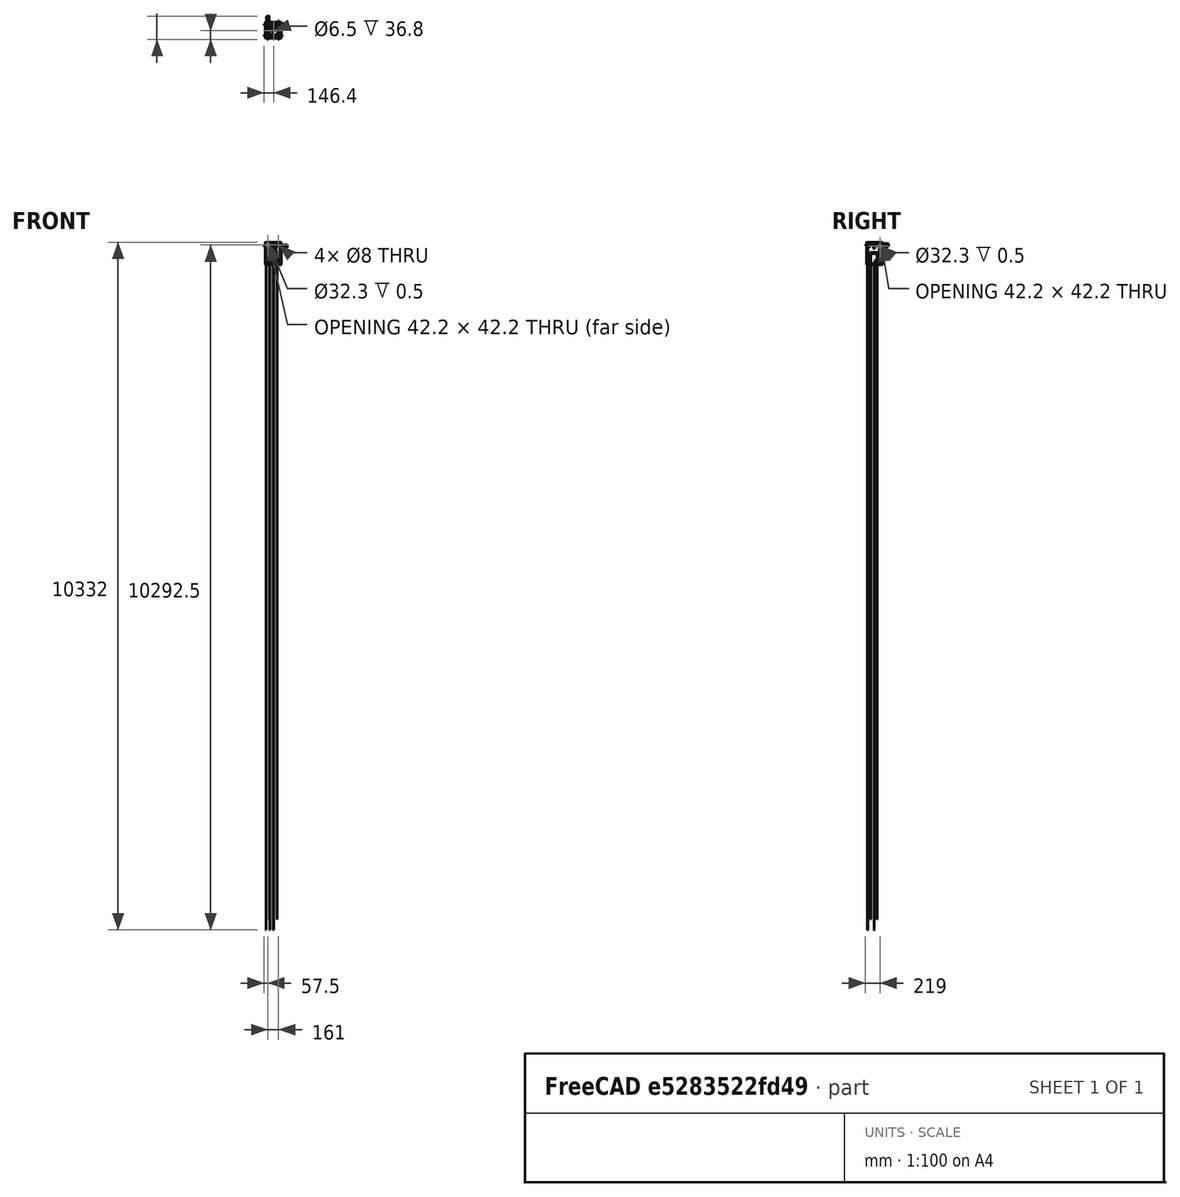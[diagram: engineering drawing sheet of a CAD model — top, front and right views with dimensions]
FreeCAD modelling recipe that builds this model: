
FCSTD DOCUMENT  (FreeCAD 0.14R3702 (Git))
Label: tantillus
License: CC-BY 3.0
LicenseURL: http://creativecommons.org/licenses/by/3.0/
objects: Mesh::Feature×42, Part::Cylinder×42, Part::Cut×35, Part::MultiFuse×16, App::DocumentObjectGroup×15, Part::FeaturePython×15, PartDesign::Pad×12, PartDesign::Chamfer×9, Sketcher::SketchObject×7, PartDesign::Pocket×6, Part::Box×5, Part::Sweep×3, Part::Chamfer×2, PartDesign::Revolution×2, Part::Helix×1
note: 175 computed .brp shape members not serialized (recipe doc carries the construction recipe); baked Part::Feature solids carry a one-line shape summary decoded from their .brp

FEATURE [PartDesign::Pad] Pad  label="Pata001"
  Length = 335
  Length2 = 100
  Type = 0
FEATURE [PartDesign::Pad] Pad001  label="Pata002"
  Length = 335
  Length2 = 100
  Placement = pos=(220,0,0) rot=(0,0,1;0rad)
  Type = 0
FEATURE [PartDesign::Pad] Pad002  label="Pata003"
  Length = 335
  Length2 = 100
  Placement = pos=(0,220,0) rot=(0,0,1;0rad)
  Type = 0
FEATURE [PartDesign::Pad] Pad003  label="Pata004"
  Length = 335
  Length2 = 100
  Placement = pos=(220,220,0) rot=(0,0,1;0rad)
  Type = 0
FEATURE [PartDesign::Pad] Pad004  label="Trab001"
  Length = 200
  Length2 = 100
  Placement = pos=(10,0,10) rot=(0,1,0;1.5708rad)
  Type = 0
FEATURE [Mesh::Feature] panel_combine_BOTTOM
  Placement = pos=(-15,-15,-15) rot=(0.57735,0.57735,0.57735;2.0944rad)
FEATURE [PartDesign::Pad] Pad005  label="Trab002"
  Length = 200
  Length2 = 100
  Placement = pos=(0,10,10) rot=(0.57735,-0.57735,-0.57735;4.18879rad)
  Type = 0
FEATURE [Mesh::Feature] panel_combine_BOTTOM001
  Placement = pos=(-15,235,-15) rot=(1,0,0;1.5708rad)
FEATURE [Mesh::Feature] panel_combine_BOTTOM002
  Placement = pos=(235,-15,-15) rot=(0,0.707107,0.707107;3.14159rad)
FEATURE [Mesh::Feature] panel_combine_BOTTOM003
  Placement = pos=(235,235,-15) rot=(0.57735,-0.57735,-0.57735;2.0944rad)
FEATURE [PartDesign::Pad] Pad006  label="Trab003"
  Length = 200
  Length2 = 100
  Placement = pos=(220,10,10) rot=(0.57735,-0.57735,-0.57735;4.18879rad)
  Type = 0
FEATURE [PartDesign::Pad] Pad007  label="Trab004"
  Length = 200
  Length2 = 100
  Placement = pos=(10,220,10) rot=(0,1,0;1.5708rad)
  Type = 0
FEATURE [PartDesign::Pad] Pad008  label="Trab005"
  Length = 200
  Length2 = 100
  Placement = pos=(10,0,325) rot=(0,1,0;1.5708rad)
  Type = 0
FEATURE [PartDesign::Pad] Pad009  label="Trab006"
  Length = 200
  Length2 = 100
  Placement = pos=(0,10,325) rot=(0.57735,-0.57735,-0.57735;4.18879rad)
  Type = 0
FEATURE [PartDesign::Pad] Pad010  label="Trab007"
  Length = 200
  Length2 = 100
  Placement = pos=(220,10,325) rot=(0.57735,-0.57735,-0.57735;4.18879rad)
  Type = 0
FEATURE [PartDesign::Pad] Pad011  label="Trab008"
  Length = 200
  Length2 = 100
  Placement = pos=(10,220,325) rot=(0,1,0;1.5708rad)
  Type = 0
FEATURE [Mesh::Feature] AnguloFrontDerecho
  Placement = pos=(50,-26,333) rot=(0,1,0;3.14159rad)
FEATURE [Mesh::Feature] AnguloFrontIzquierdo
  Placement = pos=(170.5,77,331) rot=(1,0,0;3.14159rad)
FEATURE [Mesh::Feature] AnguloTraseroDerecho
  Placement = pos=(50,143,331) rot=(0,1,0;3.14159rad)
FEATURE [Mesh::Feature] AnguloTraseroIzq
  Placement = pos=(240,162,331) rot=(0,1,0;3.14159rad)
FEATURE [App::DocumentObjectGroup] Grupo  label="T-Slot"
  Group = -> [Pad006,Pad007,Pad008,Pad009,Pad010,Pad011,Pad005,Pad,Pad001,Pad002,Pad003,Pad004]
FEATURE [App::DocumentObjectGroup] Grupo001  label="AngulosSup"
  Group = -> [AnguloFrontDerecho,AnguloFrontIzquierdo,AnguloTraseroDerecho,AnguloTraseroIzq]
FEATURE [App::DocumentObjectGroup] Grupo002  label="AngulosInf"
  Group = -> [panel_combine_BOTTOM,panel_combine_BOTTOM001,panel_combine_BOTTOM002,panel_combine_BOTTOM003]
FEATURE [Mesh::Feature] z_upper_adapter_long
  Placement = pos=(102,256.5,333) rot=(1,0,0;3.14159rad)
FEATURE [Mesh::Feature] z_lower_adapter
  Placement = pos=(122,233,-27) rot=(0,0,1;3.14159rad)
FEATURE [PartDesign::Chamfer] Chamfer001
  Placement = pos=(29.5,234,295.5) rot=(0,0,1;0rad)
  Size = 0.25
FEATURE [PartDesign::Chamfer] Chamfer
  Placement = pos=(29.5,-14,295.5) rot=(0,0,1;0rad)
  Size = 0.25
FEATURE [PartDesign::Chamfer] Chamfer002
  Placement = pos=(190.5,-14,295.5) rot=(0,0,1;0rad)
  Size = 0.25
FEATURE [PartDesign::Chamfer] Chamfer003
  Placement = pos=(190.5,234,295.5) rot=(0,0,1;0rad)
  Size = 0.25
FEATURE [App::DocumentObjectGroup] Grupo003  label="rodamientosX"
  Group = -> [Chamfer001,Chamfer,Chamfer002,Chamfer003]
FEATURE [PartDesign::Chamfer] Chamfer004
  Placement = pos=(-14,29.5,275.5) rot=(0,0,1;1.5708rad)
  Size = 0.25
FEATURE [PartDesign::Chamfer] Chamfer005
  Placement = pos=(234.5,29.5,275.5) rot=(0,0,1;1.5708rad)
  Size = 0.25
FEATURE [PartDesign::Chamfer] Chamfer006
  Placement = pos=(234.5,191,275.5) rot=(0,0,1;1.5708rad)
  Size = 0.25
FEATURE [PartDesign::Chamfer] Chamfer007
  Placement = pos=(-14,191,275.5) rot=(0,0,1;1.5708rad)
  Size = 0.25
FEATURE [App::DocumentObjectGroup] Grupo004  label="rodamientosY"
  Group = -> [Chamfer004,Chamfer005,Chamfer006,Chamfer007]
FEATURE [PartDesign::Pocket] Pocket006
  Length = 3
  Type = 0
FEATURE [Part::FeaturePython] refine  label="motor"  # WARN: FeaturePython — macro-defined, semantics opaque (R4)
  Base = -> Pocket006
  Placement = pos=(322,191,275.5) rot=(0,-1,0;1.5708rad)
FEATURE [Part::Cylinder] Cylinder  label="Cilindro"
  Angle = 360
  Height = 40
  Placement = pos=(0,0,0) rot=(0,1,0;1.5708rad)
  Radius = 2.5
FEATURE [Part::Cylinder] Cylinder001  label="Cilindro001"
  Angle = 360
  Height = 44
  Placement = pos=(-2,0,0) rot=(0,1,0;1.5708rad)
  Radius = 1.5
FEATURE [Part::Cut] Cut  label="soporte1"
  Base = -> Cylinder
  Placement = pos=(235,175.5,291) rot=(0,0,1;0rad)
  Tool = -> Cylinder001
FEATURE [Part::Cylinder] Cylinder002  label="Cilindro002"
  Angle = 360
  Height = 40
  Placement = pos=(0,0,0) rot=(0,1,0;1.5708rad)
  Radius = 2.5
FEATURE [Part::Cylinder] Cylinder003  label="Cilindro003"
  Angle = 360
  Height = 44
  Placement = pos=(-2,0,0) rot=(0,1,0;1.5708rad)
  Radius = 1.5
FEATURE [Part::Cut] Cut001  label="soporte2"
  Base = -> Cylinder002
  Placement = pos=(235,206.5,291) rot=(0,0,1;0rad)
  Tool = -> Cylinder003
FEATURE [Part::Cylinder] Cylinder004  label="Cilindro004"
  Angle = 360
  Height = 40
  Placement = pos=(0,0,0) rot=(0,1,0;1.5708rad)
  Radius = 2.5
FEATURE [Part::Cylinder] Cylinder005  label="Cilindro005"
  Angle = 360
  Height = 44
  Placement = pos=(-2,0,0) rot=(0,1,0;1.5708rad)
  Radius = 1.5
FEATURE [Part::Cut] Cut002  label="soporte3"
  Base = -> Cylinder004
  Placement = pos=(235,175.5,260) rot=(0,0,1;0rad)
  Tool = -> Cylinder005
FEATURE [Part::Cylinder] Cylinder006  label="Cilindro006"
  Angle = 360
  Height = 40
  Placement = pos=(0,0,0) rot=(0,1,0;1.5708rad)
  Radius = 2.5
FEATURE [Part::Cylinder] Cylinder007  label="Cilindro007"
  Angle = 360
  Height = 44
  Placement = pos=(-2,0,0) rot=(0,1,0;1.5708rad)
  Radius = 1.5
FEATURE [Part::Cut] Cut003  label="soporte4"
  Base = -> Cylinder006
  Placement = pos=(235,206.5,260) rot=(0,0,1;0rad)
  Tool = -> Cylinder007
FEATURE [Part::Cylinder] Cylinder008  label="barraM8Ymotor"
  Angle = 360
  Height = 276
  Placement = pos=(-28,191,275.5) rot=(0,1,0;1.5708rad)
  Radius = 4
FEATURE [Mesh::Feature] Ruedecilla
  Placement = pos=(-37,178.5,281) rot=(0,1,0;1.5708rad)
FEATURE [Part::Cut] Cut004  label="soporte005"
  Base = -> Cylinder004
  Placement = pos=(45,235,280) rot=(0,0,1;1.5708rad)
  Tool = -> Cylinder005
FEATURE [Part::Cut] Cut005  label="soporte006"
  Base = -> Cylinder002
  Placement = pos=(14,235,311) rot=(0,0,1;1.5708rad)
  Tool = -> Cylinder003
FEATURE [Part::Cut] Cut006  label="soporte007"
  Base = -> Cylinder
  Placement = pos=(45,235,311) rot=(0,0,1;1.5708rad)
  Tool = -> Cylinder001
FEATURE [Part::FeaturePython] refine001  label="motor001"  # WARN: FeaturePython — macro-defined, semantics opaque (R4)
  Base = -> Pocket006
  Placement = pos=(29.5,322,295.5) rot=(0.57735,-0.57735,0.57735;2.0944rad)
FEATURE [Part::Cut] Cut007  label="soporte008"
  Base = -> Cylinder006
  Placement = pos=(14,235,280) rot=(0,0,1;1.5708rad)
  Tool = -> Cylinder007
FEATURE [Mesh::Feature] Ruedecilla001
  Placement = pos=(42,-37,301) rot=(0.57735,-0.57735,-0.57735;4.18879rad)
FEATURE [Part::Cylinder] Cylinder009  label="barraM8Xmotor"
  Angle = 360
  Height = 276
  Placement = pos=(29.5,-28,295.5) rot=(-0.57735,0.57735,0.57735;2.0944rad)
  Radius = 4
FEATURE [Part::Cylinder] Cylinder010  label="barraM8Y"
  Angle = 360
  Height = 276
  Placement = pos=(-28,29.5,275.5) rot=(0,1,0;1.5708rad)
  Radius = 4
FEATURE [Mesh::Feature] Ruedecilla002
  Placement = pos=(-37,17,281) rot=(0,1,0;1.5708rad)
FEATURE [Part::Cylinder] Cylinder011  label="barraM8X"
  Angle = 360
  Height = 276
  Placement = pos=(190.5,-28,295.5) rot=(0.57735,-0.57735,-0.57735;4.18879rad)
  Radius = 4
FEATURE [Mesh::Feature] Ruedecilla003
  Placement = pos=(203,-37,301) rot=(0.57735,-0.57735,-0.57735;4.18879rad)
FEATURE [Mesh::Feature] Ruedecilla004
  Placement = pos=(257,17,270) rot=(0,-1,0;1.5708rad)
FEATURE [Mesh::Feature] Ruedecilla005
  Placement = pos=(203,257,290) rot=(0.57735,-0.57735,0.57735;2.0944rad)
FEATURE [App::DocumentObjectGroup] Grupo006  label="barras"
  Group = -> [Cylinder008,Ruedecilla,Cylinder009,Ruedecilla001,Cylinder010,Ruedecilla002,Cylinder011,Ruedecilla003,Ruedecilla004,Ruedecilla005]
FEATURE [Mesh::Feature] Bowden_clamp  label="Bowden clamp"
  Placement = pos=(118.4,102,304.5) rot=(0,0,1;0rad)
FEATURE [Mesh::Feature] printable_lm8uu_v  label="printable-lm8uu1"
  Placement = pos=(110.3,122.1,282.6) rot=(0.57735,-0.57735,-0.57735;2.0944rad)
FEATURE [Mesh::Feature] Carriage_bottom  label="Carriage bottom"
  Placement = pos=(-12.5,110.5,285.5) rot=(0,1,0;1.5708rad)
FEATURE [Mesh::Feature] Carriage_top  label="Carriage top"
  Placement = pos=(112.3,233,285.5) rot=(0.57735,0.57735,-0.57735;2.0944rad)
FEATURE [Mesh::Feature] printable_lm8uu_v001  label="printable-lm8uu2"
  Placement = pos=(106.2,108,296.1) rot=(0.57735,0.57735,-0.57735;2.0944rad)
FEATURE [Part::Cylinder] Cylinder012  label="barraX"
  Angle = 360
  Height = 175
  Placement = pos=(100,198,294.5) rot=(0.57735,0.57735,-0.57735;2.0944rad)
  Radius = 4
FEATURE [Part::Cylinder] Cylinder013  label="barraY"
  Angle = 360
  Height = 175
  Placement = pos=(197.3,120.5,276.4) rot=(0.57735,-0.57735,-0.57735;2.0944rad)
  Radius = 4
FEATURE [App::DocumentObjectGroup] Grupo009  label="carro"
  Group = -> [Bowden_clamp,printable_lm8uu_v,Carriage_bottom,Carriage_top,printable_lm8uu_v001,Cylinder012,Cylinder013]
FEATURE [Mesh::Feature] XY_end_left
  Placement = pos=(-23,-51.5,255) rot=(0,1,0;1.5708rad)
FEATURE [Mesh::Feature] XY_end_right
  Placement = pos=(110,110,163) rot=(0,0,1;0rad)
FEATURE [Mesh::Feature] printable_lm8uu_v002  label="printable-lm8uu003"
  Placement = pos=(105,31.1,281.8) rot=(0.57735,-0.57735,-0.57735;2.0944rad)
FEATURE [Mesh::Feature] printable_lm8uu_v003  label="printable-lm8uu004"
  Placement = pos=(106,192.6,281.7) rot=(0.57735,-0.57735,-0.57735;2.0944rad)
FEATURE [Mesh::Feature] printable_lm8uu_v004  label="printable-lm8uu005"
  Placement = pos=(27.9,114.5,289.3) rot=(-1,0,0;1.5708rad)
FEATURE [Mesh::Feature] printable_lm8uu_v005  label="printable-lm8uu006"
  Placement = pos=(188.9,115.5,289.2) rot=(-1,0,0;1.5708rad)
FEATURE [Mesh::Feature] XY_end_right001
  Placement = pos=(110.5,110.5,408) rot=(0.707107,-0.707107,0;3.14159rad)
FEATURE [Mesh::Feature] XY_end_left001
  Placement = pos=(271.5,243.5,316) rot=(0.57735,-0.57735,0.57735;2.0944rad)
FEATURE [App::DocumentObjectGroup] Grupo010  label="estremos"
  Group = -> [XY_end_left,XY_end_right,printable_lm8uu_v002,printable_lm8uu_v003,printable_lm8uu_v004,printable_lm8uu_v005,XY_end_right001,XY_end_left001]
FEATURE [Mesh::Feature] SoporteMotorEjeYFijo  label="SoporteMotorEjeZFijo"
  Placement = pos=(69,210.5,20) rot=(0,0,-1;1.5708rad)
FEATURE [Mesh::Feature] SoporteSuperiorEjeYFijo  label="SoporteSuperiorEjeZFijo"
  Placement = pos=(69,210,95) rot=(0,0,-1;1.5708rad)
FEATURE [Part::Cylinder] Cylinder014  label="barraM8008"
  Angle = 360
  Height = 225
  Placement = pos=(77,183.3,23) rot=(0,0,1;0rad)
  Radius = 4
FEATURE [Part::Cylinder] Cylinder015  label="barraM8009"
  Angle = 360
  Height = 225
  Placement = pos=(147,183.3,23) rot=(0,0,1;0rad)
  Radius = 4
FEATURE [Mesh::Feature] Z_arm_  label="Z_arm_1"
  Placement = pos=(87,108,88) rot=(0.57735,-0.57735,-0.57735;2.0944rad)
FEATURE [Mesh::Feature] Z_arm_001  label="Z_arm_2"
  Placement = pos=(137,108,88) rot=(0.57735,-0.57735,0.57735;4.18879rad)
FEATURE [Mesh::Feature] Z_lift
  Placement = pos=(107,253.5,219.1) rot=(0,0,1;1.5708rad)
FEATURE [Mesh::Feature] printable_lm8uu_v006  label="printable-lm8uu-v3"
  Placement = pos=(145.3,189.5,110) rot=(0,0,1;0rad)
FEATURE [Mesh::Feature] printable_lm8uu_v007  label="printable-lm8uu-v004"
  Placement = pos=(145.3,189.5,163) rot=(0,0,1;0rad)
FEATURE [Mesh::Feature] printable_lm8uu_v008  label="printable-lm8uu-v005"
  Placement = pos=(75.4,189.5,163) rot=(0,0,1;0rad)
FEATURE [Mesh::Feature] printable_lm8uu_v009  label="printable-lm8uu-v006"
  Placement = pos=(75.4,189.5,110) rot=(0,0,1;0rad)
FEATURE [Part::Box] Box  label="tablelisa"
  Height = 3
  Length = 120
  Placement = pos=(53,45,161) rot=(0,0,1;0rad)
  Width = 120
FEATURE [Part::FeaturePython] refine002  label="motor002"  # WARN: FeaturePython — macro-defined, semantics opaque (R4)
  Placement = pos=(123.06,123.895,42) rot=(-0.987266,-0.112485,0.112485;1.58361rad)
FEATURE [Mesh::Feature] Z_lift001
  Placement = pos=(96,90,163.6) rot=(0,0,-1;1.5708rad)
FEATURE [Mesh::Feature] Z_lift_tensioner
  Placement = pos=(113,239.7,126.3) rot=(0.519988,-0.519988,-0.677661;1.95044rad)
FEATURE [App::DocumentObjectGroup] Grupo012  label="lift cordel"
  Group = -> [Z_lift001,Z_lift_tensioner]
FEATURE [Part::Cylinder] Cylinder016  label="Cilindro008"
  Angle = 360
  Height = 10
  Placement = pos=(79.5,114.1,158) rot=(0,0,1;0rad)
  Radius = 2.6
FEATURE [Part::Cylinder] Cylinder017  label="Cilindro009"
  Angle = 360
  Height = 10
  Placement = pos=(144.5,114.1,158) rot=(0,0,1;0rad)
  Radius = 2.6
FEATURE [Part::Cylinder] Cylinder018  label="Cilindro010"
  Angle = 360
  Height = 10
  Placement = pos=(144.5,152.1,158) rot=(0,0,1;0rad)
  Radius = 2.6
FEATURE [Part::Cylinder] Cylinder019  label="Cilindro011"
  Angle = 360
  Height = 10
  Placement = pos=(79.5,152.1,158) rot=(0,0,1;0rad)
  Radius = 2.6
FEATURE [Part::Cut] Cut008
  Base = -> Box
  Tool = -> Cylinder016
FEATURE [Part::Cut] Cut009
  Base = -> Cut008
  Tool = -> Cylinder017
FEATURE [Part::Cut] Cut010
  Base = -> Cut009
  Tool = -> Cylinder019
FEATURE [Part::Cut] Cut011  label="mesainf01"
  Base = -> Cut010
  Tool = -> Cylinder018
FEATURE [Part::Box] Box001  label="tablelisa001"
  Height = 3
  Length = 120
  Placement = pos=(53,45,174) rot=(0,0,1;0rad)
  Width = 120
FEATURE [Sketcher::SketchObject] Sketch
  Placement = pos=(53,45,177) rot=(0,0,1;0rad)
  Support = -> Box001 [Face6]
  sketch-geometry (3):
    g0: Circle CenterX=5 CenterY=5 CenterZ=0 NormalX=0 NormalY=0 NormalZ=1 Radius=1.5
    g1: Circle CenterX=115 CenterY=5 CenterZ=0 NormalX=0 NormalY=0 NormalZ=1 Radius=1.5
    g2: Circle CenterX=60 CenterY=105 CenterZ=0 NormalX=0 NormalY=0 NormalZ=1 Radius=1.5
  constraints (9):
    c: Equal(g2,g1)
    c: Equal(g1,g0)
    c: Radius(g0) = 1.5
    c: DistanceY(g-1,g0) = 5
    c: DistanceX(g-1,g0) = 5
    c: DistanceY(g-1,g1) = 5
    c: DistanceX(g-1,g1) = 115
    c: DistanceY(g-1,g2) = 105
    c: DistanceX(g-1,g2) = 60
FEATURE [PartDesign::Pocket] Pocket  label="mesasup"
  Length = 5
  Placement = pos=(53,45,174) rot=(0,0,1;0rad)
  Sketch = -> Sketch
  Type = 1
FEATURE [Sketcher::SketchObject] Sketch001
  ExternalGeometry = -> [Cut011]
  Placement = pos=(0,0,164) rot=(0,0,1;0rad)
  Support = -> Cut011 [Face3]
  sketch-geometry (3):
    g0: Circle CenterX=58 CenterY=50 CenterZ=0 NormalX=0 NormalY=0 NormalZ=1 Radius=1.5
    g1: Circle CenterX=168 CenterY=50 CenterZ=0 NormalX=0 NormalY=0 NormalZ=1 Radius=1.5
    g2: Circle CenterX=113 CenterY=150 CenterZ=0 NormalX=0 NormalY=0 NormalZ=1 Radius=1.5
  constraints (9):
    c: Equal(g2,g1)
    c: Equal(g1,g0)
    c: Radius(g1) = 1.5
    c: DistanceX(g0,g-4) = -5
    c: DistanceY(g0,g-4) = -5
    c: DistanceX(g1,g-4) = 5
    c: DistanceY(g1,g-4) = -5
    c: DistanceX(g2,g-3) = -60
    c: DistanceY(g2,g-3) = 15
FEATURE [PartDesign::Pocket] Pocket007  label="mesainf"
  Length = 5
  Sketch = -> Sketch001
  Type = 1
FEATURE [Part::Cylinder] Cylinder020  label="Cilindro012"
  Angle = 360
  Height = 22
  Radius = 1.5
FEATURE [Part::Chamfer] Chamfer008
  Base = -> Cylinder020
  Edges = 1 edges r=0.2: [Edge3]
FEATURE [Part::Cylinder] Cylinder021  label="Cilindro013"
  Angle = 360
  Height = 3
  Placement = pos=(0,0,21) rot=(0,0,1;0rad)
  Radius = 2
FEATURE [Part::Chamfer] Chamfer009
  Base = -> Cylinder021
  Edges = 1 edges r=0.2: [Edge1]
FEATURE [Part::MultiFuse] Fusion
  Shapes = -> [Chamfer008,Chamfer009]
FEATURE [Sketcher::SketchObject] Sketch002
  Placement = pos=(0,0,24) rot=(0,0,1;0rad)
  Support = -> Fusion [Face7]
  sketch-geometry (7):
    g0: LineSegment StartX=-1.25 StartY=0.721688 StartZ=0 EndX=0 EndY=1.44338 EndZ=0
    g1: LineSegment StartX=0 StartY=1.44338 StartZ=0 EndX=1.25 EndY=0.721688 EndZ=0
    g2: LineSegment StartX=1.25 StartY=0.721688 StartZ=0 EndX=1.25 EndY=-0.721688 EndZ=0
    g3: LineSegment StartX=1.25 StartY=-0.721688 StartZ=0 EndX=0 EndY=-1.44338 EndZ=0
    g4: LineSegment StartX=0 StartY=-1.44338 StartZ=0 EndX=-1.25 EndY=-0.721688 EndZ=0
    g5: LineSegment StartX=-1.25 StartY=-0.721688 StartZ=0 EndX=-1.25 EndY=0.721688 EndZ=0
    g6: LineSegment [constr] StartX=0 StartY=1.44338 StartZ=0 EndX=0 EndY=0 EndZ=0
  constraints (20):
    c: PointOnObject(g0,g-2)
    c: Coincident(g0,g1)
    c: Coincident(g1,g2)
    c: Vertical(g2)
    c: Coincident(g2,g3)
    c: PointOnObject(g3,g-2)
    c: Coincident(g3,g4)
    c: Coincident(g4,g5)
    c: Coincident(g5,g0)
    c: Vertical(g5)
    c: Equal(g5,g0)
    c: Equal(g0,g1)
    c: Equal(g1,g2)
    c: Equal(g2,g3)
    c: Equal(g3,g4)
    c: Coincident(g6,g0)
    c: Coincident(g6,g-1)
    c: Angle(g0,g6) = 1.0472
    c: Symmetric(g0,g3,g-1)
    c: DistanceX(g2,g4) = -2.5
FEATURE [PartDesign::Pocket] Pocket008
  Length = 2
  Sketch = -> Sketch002
  Type = 0
FEATURE [Part::Cylinder] Cylinder022  label="Cilindro014"
  Angle = 360
  Height = 0.3
  Placement = pos=(0,0,20.7) rot=(0,0,1;0rad)
  Radius = 3
FEATURE [Part::MultiFuse] Fusion001
  Shapes = -> [Cylinder022,Pocket008]
FEATURE [Part::Cylinder] Cylinder023  label="Cilindro015"
  Angle = 360
  Height = 0.3
  Placement = pos=(0,0,17.4) rot=(0,0,1;0rad)
  Radius = 3
FEATURE [Part::MultiFuse] Fusion002
  Shapes = -> [Cylinder023,Fusion001]
FEATURE [Part::Cylinder] Cylinder024  label="Cilindro016"
  Angle = 360
  Height = 0.3
  Placement = pos=(0,0,7.7) rot=(0,0,1;0rad)
  Radius = 3
FEATURE [Part::MultiFuse] Fusion003
  Shapes = -> [Cylinder024,Fusion002]
FEATURE [Part::Cylinder] Cylinder025  label="Cilindro017"
  Angle = 360
  Height = 0.3
  Placement = pos=(0,0,4.4) rot=(0,0,1;0rad)
  Radius = 3
FEATURE [Part::MultiFuse] Fusion004
  Shapes = -> [Fusion003,Cylinder025]
FEATURE [Part::Helix] Helix  label="Muelletrazo"
  Angle = 0
  Height = 9.4
  LocalCoord = 0
  Pitch = 1
  Placement = pos=(0,0,8) rot=(0,0,1;0rad)
  Radius = 2.5
  Style = 1
FEATURE [Sketcher::SketchObject] Sketch003
  Placement = pos=(0,0,0) rot=(1,0,0;1.5708rad)
  sketch-geometry (1):
    g0: Circle CenterX=2.5 CenterY=8 CenterZ=0 NormalX=0 NormalY=0 NormalZ=1 Radius=0.1
  constraints (3):
    c: Radius(g0) = 0.1
    c: DistanceX(g-1,g0) = 2.5
    c: DistanceY(g-1,g0) = 8
FEATURE [Part::Sweep] Sweep
  Frenet = true
  Sections = -> [Sketch003]
  Solid = true
  Spine = -> Helix [Edge1]
  Transition = 1
FEATURE [Part::MultiFuse] Fusion005  label="tonillocama"
  Placement = pos=(58,50,156.3) rot=(0,0,1;0rad)
  Shapes = -> [Fusion004,Sweep]
FEATURE [Part::Sweep] Sweep001
  Frenet = true
  Sections = -> [Sketch003]
  Solid = true
  Spine = -> Helix [Edge1]
  Transition = 1
FEATURE [Part::MultiFuse] Fusion006
  Shapes = -> [Fusion003,Cylinder025]
FEATURE [Part::MultiFuse] Fusion007  label="tonillocama001"
  Placement = pos=(168,50,156.3) rot=(0,0,1;0rad)
  Shapes = -> [Fusion006,Sweep001]
FEATURE [Part::MultiFuse] Fusion008
  Shapes = -> [Fusion003,Cylinder025]
FEATURE [Part::Sweep] Sweep002
  Frenet = true
  Sections = -> [Sketch003]
  Solid = true
  Spine = -> Helix [Edge1]
  Transition = 1
FEATURE [Part::MultiFuse] Fusion009  label="tonillocama002"
  Placement = pos=(113,150,156.3) rot=(0,0,1;0rad)
  Shapes = -> [Fusion008,Sweep002]
FEATURE [Part::Cylinder] Cylinder026  label="Cilindro018"
  Angle = 360
  Height = 3
  Radius = 7
FEATURE [Sketcher::SketchObject] Sketch004  label="PasoTuerca"
  Placement = pos=(0,0,3) rot=(0,0,1;0rad)
  Support = -> Cylinder026 [Face2]
  sketch-geometry (8):
    g0: LineSegment StartX=-3.46409 StartY=0 StartZ=0 EndX=-1.73205 EndY=3 EndZ=0
    g1: LineSegment StartX=-1.73205 StartY=3 StartZ=0 EndX=1.73205 EndY=3 EndZ=0
    g2: LineSegment StartX=1.73205 StartY=3 StartZ=0 EndX=3.46409 EndY=0 EndZ=0
    g3: LineSegment StartX=3.46409 StartY=0 StartZ=0 EndX=1.73205 EndY=-3 EndZ=0
    g4: LineSegment StartX=1.73205 StartY=-3 StartZ=0 EndX=-1.73205 EndY=-3 EndZ=0
    g5: LineSegment StartX=-1.73205 StartY=-3 StartZ=0 EndX=-3.46409 EndY=0 EndZ=0
    g6: LineSegment [constr] StartX=-3.46409 StartY=0 StartZ=0 EndX=0 EndY=0 EndZ=0
    g7: LineSegment [constr] StartX=-1.73205 StartY=3 StartZ=0 EndX=0 EndY=0 EndZ=0
  constraints (21):
    c: Coincident(g0,g1)
    c: Coincident(g1,g2)
    c: Coincident(g2,g3)
    c: Coincident(g3,g4)
    c: Coincident(g4,g5)
    c: Coincident(g5,g0)
    c: Equal(g5,g0)
    c: Equal(g0,g1)
    c: Equal(g1,g2)
    c: Equal(g2,g3)
    c: Equal(g3,g4)
    c: Coincident(g6,g0)
    c: Horizontal(g1)
    c: Horizontal(g4)
    c: DistanceY(g0,g4) = -6
    c: Symmetric(g4,g0,g6)
    c: Symmetric(g0,g2,g6)
    c: Coincident(g7,g0)
    c: Coincident(g7,g6)
    c: Angle(g7,g6) = 1.0472
    c: Coincident(g6,g-1)
FEATURE [PartDesign::Pocket] Pocket009
  Length = 2
  Sketch = -> Sketch004
  Type = 0
FEATURE [App::DocumentObjectGroup] Grupo013  label="ocultar"
  Group = -> [Box,Z_lift,Box001,Cut011,Fusion,Helix,Pocket009,Cylinder026]
FEATURE [PartDesign::Chamfer] Chamfer010
  Base = -> Pocket009 [Edge1]
  Size = 1
FEATURE [Part::Cylinder] Cylinder027  label="Cilindro019"
  Angle = 360
  Height = 10
  Placement = pos=(0,0,-2) rot=(0,0,1;0rad)
  Radius = 1.5
FEATURE [Part::Cut] Cut012
  Base = -> Chamfer010
  Tool = -> Cylinder027
FEATURE [Part::Cylinder] Cylinder028  label="Cilindro020"
  Angle = 360
  Height = 10
  Placement = pos=(7,0,-2) rot=(0,0,1;0rad)
  Radius = 1
FEATURE [Part::FeaturePython] Array  # Draft array (typed FeaturePython)
  Angle = 360
  ArrayType = 1
  Axis = (0,0,1)
  Base = -> Cylinder028
  Center = (0,0,0)
  IntervalX = (1,0,0)
  IntervalY = (0,1,0)
  IntervalZ = (0,0,1)
  NumberPolar = 12
  NumberX = 2
  NumberY = 2
  NumberZ = 1
FEATURE [Part::Cut] Cut013
  Base = -> Cut012
  Placement = pos=(58,50,157) rot=(0,0,1;0rad)
  Tool = -> Array
FEATURE [Part::Cut] Cut014
  Base = -> Chamfer010
  Tool = -> Cylinder027
FEATURE [Part::FeaturePython] Array001  # Draft array (typed FeaturePython)
  Angle = 360
  ArrayType = 1
  Axis = (0,0,1)
  Base = -> Cylinder028
  Center = (0,0,0)
  IntervalX = (1,0,0)
  IntervalY = (0,1,0)
  IntervalZ = (0,0,1)
  NumberPolar = 12
  NumberX = 2
  NumberY = 2
  NumberZ = 1
FEATURE [Part::Cut] Cut015
  Base = -> Cut014
  Placement = pos=(168,50,157) rot=(0,0,1;0rad)
  Tool = -> Array001
FEATURE [Part::Cut] Cut016
  Base = -> Chamfer010
  Tool = -> Cylinder027
FEATURE [Part::FeaturePython] Array002  # Draft array (typed FeaturePython)
  Angle = 360
  ArrayType = 1
  Axis = (0,0,1)
  Base = -> Cylinder028
  Center = (0,0,0)
  IntervalX = (1,0,0)
  IntervalY = (0,1,0)
  IntervalZ = (0,0,1)
  NumberPolar = 12
  NumberX = 2
  NumberY = 2
  NumberZ = 1
FEATURE [Part::Cut] Cut017
  Base = -> Cut016
  Placement = pos=(113,150,157) rot=(0,0,1;0rad)
  Tool = -> Array002
FEATURE [Part::Box] Box002  label="metraquilato"
  Height = 5
  Length = 125
  Placement = pos=(50.5,42.5,177.1) rot=(0,0,1;0rad)
  Width = 125
FEATURE [App::DocumentObjectGroup] Grupo011  label="EjeZ"
  Group = -> [SoporteMotorEjeYFijo,SoporteSuperiorEjeYFijo,Cylinder014,Cylinder015,Z_arm_,Z_arm_001,printable_lm8uu_v006,printable_lm8uu_v007,printable_lm8uu_v008,printable_lm8uu_v009,refine002,Grupo012,z_upper_adapter_long,z_lower_adapter,Pocket,Pocket007,Fusion005,Fusion007,Fusion009,Cut013,Cut015,Cut017,Box002]
FEATURE [Part::Cylinder] Cylinder029  label="Cilindro021"
  Angle = 360
  Height = 40
  Radius = 8
FEATURE [Part::Cylinder] Cylinder030  label="Cilindro022"
  Angle = 360
  Height = 4.6
  Radius = 8
FEATURE [Part::Cylinder] Cylinder031  label="Cilindro023"
  Angle = 360
  Height = 10
  Placement = pos=(0,0,-2) rot=(0,0,1;0rad)
  Radius = 6
FEATURE [Part::Cut] Cut018
  Base = -> Cylinder030
  Placement = pos=(0,0,30.6) rot=(0,0,1;0rad)
  Tool = -> Cylinder031
FEATURE [Part::Cut] Cut019
  Base = -> Cylinder029
  Tool = -> Cut018
FEATURE [Part::Cylinder] Cylinder032  label="Cilindro024"
  Angle = 360
  Height = 42
  Placement = pos=(0,0,-1) rot=(0,0,1;0rad)
  Radius = 3.25
FEATURE [Part::Cut] Cut020
  Base = -> Cut019
  Tool = -> Cylinder032
FEATURE [Part::Cylinder] Cylinder033  label="Cilindro025"
  Angle = 360
  Height = 4.2
  Placement = pos=(0,0,-1) rot=(0,0,1;0rad)
  Radius = 4
FEATURE [Sketcher::SketchObject] Sketch005
  Placement = pos=(0,0,0) rot=(1,0,0;1.5708rad)
  sketch-geometry (4):
    g0: LineSegment [constr] StartX=-5 StartY=0 StartZ=0 EndX=5 EndY=0 EndZ=0
    g1: LineSegment StartX=-11.6906 StartY=3.86281 StartZ=0 EndX=-1.29847 EndY=-2.13708 EndZ=0
    g2: LineSegment StartX=-11.6906 StartY=-2.13708 StartZ=0 EndX=-11.6906 EndY=3.86281 EndZ=0
    g3: LineSegment StartX=-11.6906 StartY=-2.13708 StartZ=0 EndX=-1.29847 EndY=-2.13708 EndZ=0
  constraints (11):
    c: PointOnObject(g0,g-1)
    c: PointOnObject(g0,g-1)
    c: DistanceX(g0,g0) = -10
    c: Coincident(g2,g1)
    c: Vertical(g2)
    c: PointOnObject(g0,g1)
    c: Symmetric(g0,g0,g-2)
    c: Coincident(g3,g2)
    c: Coincident(g3,g1)
    c: Horizontal(g3)
    c: Angle(g0,g1) = 2.61799
FEATURE [Part::Cut] Cut021
  Base = -> Cut020
  Tool = -> Cylinder033
FEATURE [PartDesign::Revolution] Revolution
  Angle = 360
  Axis = (0,0,1)
  Base = (0,0,0)
  Placement = pos=(0,0,0) rot=(1,0,0;1.5708rad)
  ReferenceAxis = -> Sketch005 [V_Axis]
  Sketch = -> Sketch005
FEATURE [Part::Cut] Cut022
  Base = -> Cut021
  Tool = -> Revolution
FEATURE [Part::Cylinder] Cylinder034  label="Cilindro026"
  Angle = 360
  Height = 10
  Placement = pos=(4.2,0,0) rot=(0,1,0;1.5708rad)
  Radius = 1
FEATURE [Part::Cylinder] Cylinder035  label="Cilindro027"
  Angle = 360
  Height = 2
  Placement = pos=(0,0,-1) rot=(0,0,1;0rad)
  Radius = 4.2
FEATURE [Part::Cylinder] Cylinder036  label="Cilindro028"
  Angle = 60
  Height = 2
  Placement = pos=(0,0,-1) rot=(0,0,1;0rad)
  Radius = 14.2
FEATURE [Part::Cut] Cut023
  Base = -> Cylinder036
  Tool = -> Cylinder035
FEATURE [Part::Cylinder] Cylinder037  label="Cilindro029"
  Angle = 360
  Height = 10
  Placement = pos=(2.1,3.63731,0) rot=(-0.447214,0.774597,0.447214;1.82348rad)
  Radius = 1
FEATURE [Part::MultiFuse] Fusion010
  Shapes = -> [Cylinder034,Cut023]
FEATURE [Part::MultiFuse] Fusion011
  Shapes = -> [Cylinder037,Fusion010]
FEATURE [Part::FeaturePython] Array003  # Draft array (typed FeaturePython)
  Angle = 360
  ArrayType = 1
  Axis = (0,0,1)
  Base = -> Fusion011
  Center = (0,0,0)
  IntervalX = (1,0,0)
  IntervalY = (0,1,0)
  IntervalZ = (0,0,1)
  NumberPolar = 4
  NumberX = 1
  NumberY = 1
  NumberZ = 1
  Placement = pos=(0,0,13.5) rot=(0,0,1;0.261799rad)
FEATURE [Part::MultiFuse] Fusion012
  Shapes = -> [Cylinder037,Fusion010]
FEATURE [Part::FeaturePython] Array004  # Draft array (typed FeaturePython)
  Angle = 360
  ArrayType = 1
  Axis = (0,0,1)
  Base = -> Fusion012
  Center = (0,0,0)
  IntervalX = (1,0,0)
  IntervalY = (0,1,0)
  IntervalZ = (0,0,1)
  NumberPolar = 4
  NumberX = 1
  NumberY = 1
  NumberZ = 1
  Placement = pos=(0,0,16.5) rot=(0,0,1;0.261799rad)
FEATURE [Part::FeaturePython] Array005  # Draft array (typed FeaturePython)
  Angle = 360
  ArrayType = 1
  Axis = (0,0,1)
  Base = -> Fusion011
  Center = (0,0,0)
  IntervalX = (1,0,0)
  IntervalY = (0,1,0)
  IntervalZ = (0,0,1)
  NumberPolar = 4
  NumberX = 1
  NumberY = 1
  NumberZ = 1
  Placement = pos=(0,0,22.5) rot=(0,0,1;0.261799rad)
FEATURE [Part::MultiFuse] Fusion013
  Shapes = -> [Cylinder037,Fusion010]
FEATURE [Part::FeaturePython] Array006  # Draft array (typed FeaturePython)
  Angle = 360
  ArrayType = 1
  Axis = (0,0,1)
  Base = -> Fusion013
  Center = (0,0,0)
  IntervalX = (1,0,0)
  IntervalY = (0,1,0)
  IntervalZ = (0,0,1)
  NumberPolar = 4
  NumberX = 1
  NumberY = 1
  NumberZ = 1
  Placement = pos=(0,0,19.5) rot=(0,0,1;0.261799rad)
FEATURE [Part::MultiFuse] Fusion014
  Shapes = -> [Cylinder037,Fusion010]
FEATURE [Part::FeaturePython] Array007  # Draft array (typed FeaturePython)
  Angle = 360
  ArrayType = 1
  Axis = (0,0,1)
  Base = -> Fusion014
  Center = (0,0,0)
  IntervalX = (1,0,0)
  IntervalY = (0,1,0)
  IntervalZ = (0,0,1)
  NumberPolar = 4
  NumberX = 1
  NumberY = 1
  NumberZ = 1
  Placement = pos=(0,0,25.5) rot=(0,0,1;0.261799rad)
FEATURE [Part::Box] Box003  label="Cubo"
  Height = 8
  Length = 3
  Placement = pos=(6.5,-10,0) rot=(0,0,1;0rad)
  Width = 20
FEATURE [Part::Box] Box004  label="Cubo001"
  Height = 8
  Length = 3
  Placement = pos=(-9.5,-10,0) rot=(0,0,1;0rad)
  Width = 20
FEATURE [Part::Cut] Cut024
  Base = -> Cut022
  Tool = -> Box003
FEATURE [Part::Cut] Cut025
  Base = -> Cut024
  Tool = -> Box004
FEATURE [Part::Cut] Cut026
  Base = -> Cut025
  Tool = -> Array003
FEATURE [Part::Cut] Cut027
  Base = -> Cut026
  Tool = -> Array004
FEATURE [Part::Cut] Cut028
  Base = -> Cut027
  Tool = -> Array007
FEATURE [Part::Cut] Cut029
  Base = -> Cut028
  Tool = -> Array006
FEATURE [Part::Cut] Cut030
  Base = -> Cut029
  Tool = -> Array005
FEATURE [Part::Cylinder] Cylinder038  label="Cilindro030"
  Angle = 360
  Height = 2
  Placement = pos=(-1,5.2,16.5) rot=(0,1,0;1.5708rad)
  Radius = 1
FEATURE [Part::FeaturePython] Array008  # Draft array (typed FeaturePython)
  Angle = 360
  ArrayType = 1
  Axis = (0,0,1)
  Base = -> Cylinder038
  Center = (0,0,0)
  IntervalX = (1,0,0)
  IntervalY = (0,1,0)
  IntervalZ = (0,0,1)
  NumberPolar = 4
  NumberX = 0
  NumberY = 0
  NumberZ = 0
FEATURE [Part::Cylinder] Cylinder039  label="Cilindro031"
  Angle = 360
  Height = 2
  Placement = pos=(-1,5.2,16.5) rot=(0,1,0;1.5708rad)
  Radius = 1
FEATURE [Part::FeaturePython] Array009  # Draft array (typed FeaturePython)
  Angle = 360
  ArrayType = 1
  Axis = (0,0,1)
  Base = -> Cylinder039
  Center = (0,0,0)
  IntervalX = (1,0,0)
  IntervalY = (0,1,0)
  IntervalZ = (0,0,1)
  NumberPolar = 4
  NumberX = 0
  NumberY = 0
  NumberZ = 0
  Placement = pos=(0,0,3) rot=(0,0,1;0rad)
FEATURE [Part::Cylinder] Cylinder040  label="Cilindro032"
  Angle = 360
  Height = 2
  Placement = pos=(-1,5.2,16.5) rot=(0,1,0;1.5708rad)
  Radius = 1
FEATURE [Part::FeaturePython] Array010  # Draft array (typed FeaturePython)
  Angle = 360
  ArrayType = 1
  Axis = (0,0,1)
  Base = -> Cylinder040
  Center = (0,0,0)
  IntervalX = (1,0,0)
  IntervalY = (0,1,0)
  IntervalZ = (0,0,1)
  NumberPolar = 4
  NumberX = 0
  NumberY = 0
  NumberZ = 0
  Placement = pos=(0,0,6) rot=(0,0,1;0rad)
FEATURE [Part::Cylinder] Cylinder041  label="Cilindro033"
  Angle = 360
  Height = 2
  Placement = pos=(-1,5.2,16.5) rot=(0,1,0;1.5708rad)
  Radius = 1
FEATURE [Part::FeaturePython] Array011  # Draft array (typed FeaturePython)
  Angle = 360
  ArrayType = 1
  Axis = (0,0,1)
  Base = -> Cylinder041
  Center = (0,0,0)
  IntervalX = (1,0,0)
  IntervalY = (0,1,0)
  IntervalZ = (0,0,1)
  NumberPolar = 4
  NumberX = 0
  NumberY = 0
  NumberZ = 0
  Placement = pos=(0,0,9) rot=(0,0,1;0rad)
FEATURE [Part::Cut] Cut031
  Base = -> Cut030
  Tool = -> Array008
FEATURE [Part::Cut] Cut032
  Base = -> Cut031
  Tool = -> Array009
FEATURE [Part::Cut] Cut033
  Base = -> Cut032
  Tool = -> Array010
FEATURE [Part::Cut] Cut034  label="cuerpo j-head"
  Base = -> Cut033
  Placement = pos=(118.4,102,252) rot=(0,0,1;0rad)
  Tool = -> Array011
FEATURE [Sketcher::SketchObject] Sketch006
  Placement = pos=(12.7,0,0) rot=(0.57735,0.57735,0.57735;2.0944rad)
  sketch-geometry (1):
    g0: Circle CenterX=12.1 CenterY=4.1 CenterZ=0 NormalX=0 NormalY=0 NormalZ=1 Radius=3
  constraints (1):
    c: Radius(g0) = 3
FEATURE [PartDesign::Pocket] Pocket010
  Length = 5
  Sketch = -> Sketch006
  Type = 1
FEATURE [PartDesign::Revolution] Revolution001
  Angle = 360
  Axis = (0,0,1)
  Base = (0,0,0)
  Placement = pos=(6.35,5,0) rot=(1,0,0;1.5708rad)
FEATURE [Part::MultiFuse] Fusion015  label="hotend"
  Placement = pos=(111.9,97,243) rot=(0,0,1;0rad)
  Shapes = -> [Pocket010,Revolution001]
FEATURE [App::DocumentObjectGroup] Grupo014  label="J-Head"
  Group = -> [Fusion015,Cut034]
FEATURE [App::DocumentObjectGroup] Grupo008  label="EjeXY"
  Group = -> [Grupo009,Grupo010,Grupo014]
FEATURE [Mesh::Feature] coupler
  Placement = pos=(240,191,275.5) rot=(0,1,0;1.5708rad)
FEATURE [App::DocumentObjectGroup] Grupo005  label="motor eje Y"
  Group = -> [refine,Cut,Cut001,Cut002,Cut003,coupler]
FEATURE [Mesh::Feature] coupler001
  Placement = pos=(29.5,269,295.5) rot=(1,0,0;1.5708rad)
FEATURE [App::DocumentObjectGroup] Grupo007  label="motor eje X"
  Group = -> [refine001,Cut006,Cut005,Cut004,Cut007,coupler001]
